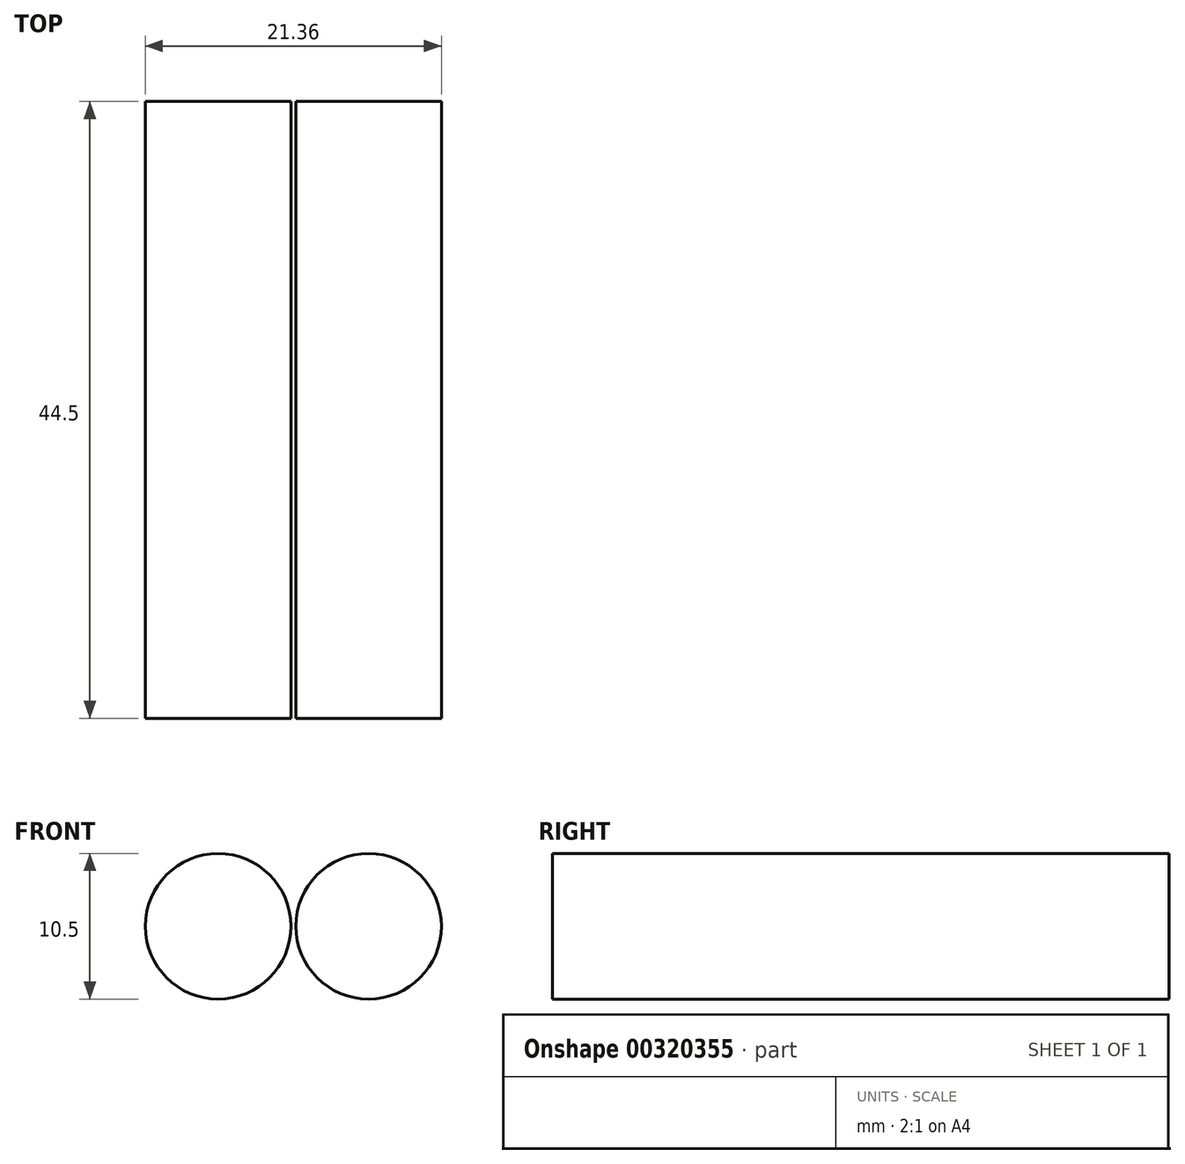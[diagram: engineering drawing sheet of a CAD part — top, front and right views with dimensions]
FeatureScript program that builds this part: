
annotation { "Feature Type Name" : "Feature", "Feature Type Description" : "" }
export const myFeature = defineFeature(function(context is Context, id is Id, definition is map)
    precondition{}
    {
        {
            var Q0;
            Q0=qCreatedBy(makeId("Front.planeOp"),FACE);
            var sketch = newSketch(context, id + "F0", { "sketchPlane" : qUnion([Q0])});
            skCircle(sketch, "E0", {"center": v(0, 0) * mm, "radius": 5.25 * mm});
            skCircle(sketch, "E1", {"center": v(-10.86, 0) * mm, "radius": 5.25 * mm});
            skSolve(sketch);
        }
        {
            var Q0;
            Q0 = qSketchRegion(id + "F0", true);
            extrude(context, id + "F1", {"entities" : qUnion([Q0]), "depth" : 22.25 * mm, "hasSecondDirection" : true, "secondDirectionOppositeDirection" : true, "secondDirectionDepth" : 22.25 * mm});
        }
    });
